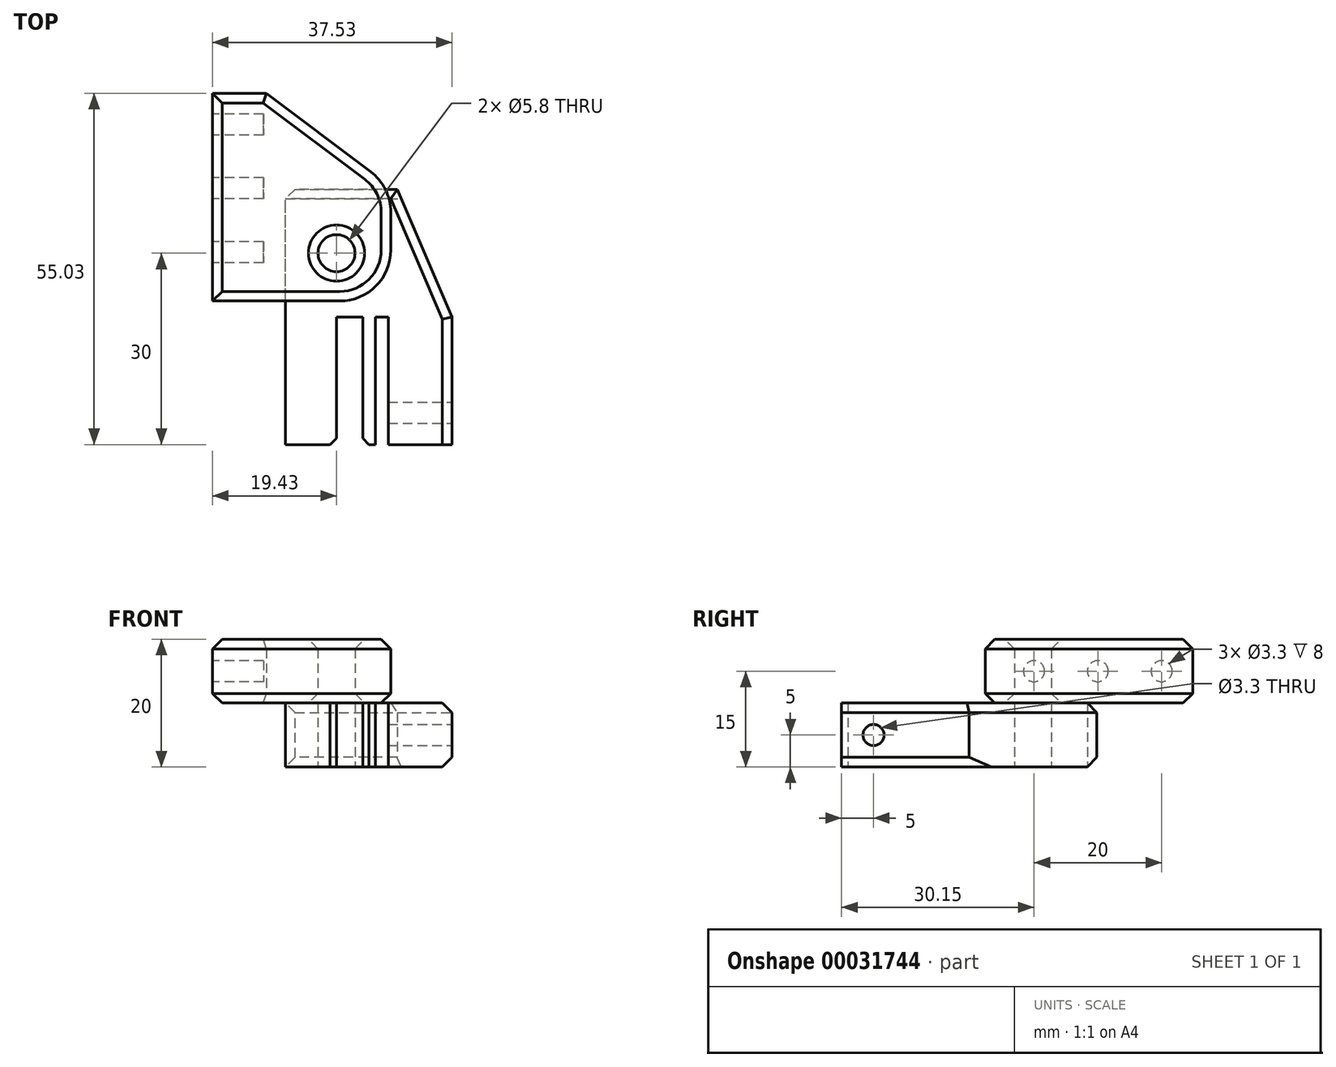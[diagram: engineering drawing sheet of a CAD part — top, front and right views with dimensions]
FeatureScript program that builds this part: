
annotation { "Feature Type Name" : "Feature", "Feature Type Description" : "" }
export const myFeature = defineFeature(function(context is Context, id is Id, definition is map)
    precondition{}
    {
        {
            var Q0;
            Q0=qCreatedBy(makeId("Top.planeOp"),FACE);
            var sketch = newSketch(context, id + "F0", { "sketchPlane" : qUnion([Q0])});
            skLineSegment(sketch, "E0", {"start": v(8, 40) * mm, "end": v(34.1, 40) * mm});
            skLineSegment(sketch, "E1", {"start": v(34.1, 40) * mm, "end": v(34.1, 0) * mm});
            skLineSegment(sketch, "E2", {"start": v(34.1, 0) * mm, "end": v(24.1, 0) * mm});
            skLineSegment(sketch, "E3", {"start": v(24.1, 0) * mm, "end": v(24.1, 20) * mm});
            skLineSegment(sketch, "E4", {"start": v(24.1, 20) * mm, "end": v(22.1, 20) * mm});
            skLineSegment(sketch, "E5", {"start": v(22.1, 20) * mm, "end": v(22.1, 0) * mm});
            skLineSegment(sketch, "E6", {"start": v(22.1, 0) * mm, "end": v(20.1, 0) * mm});
            skLineSegment(sketch, "E7", {"start": v(20.1, 0) * mm, "end": v(20.1, 20) * mm});
            skLineSegment(sketch, "E8", {"start": v(20.1, 20) * mm, "end": v(16, 20) * mm});
            skLineSegment(sketch, "E9", {"start": v(16, 20) * mm, "end": v(16, 0) * mm});
            skLineSegment(sketch, "E10", {"start": v(16, 0) * mm, "end": v(8, 0) * mm});
            skPoint(sketch, "E11.orphan", {"position": v(0, 0) * mm});
            skLineSegment(sketch, "E12", {"start": v(8, 0) * mm, "end": v(8, 40) * mm});
            skSolve(sketch);
        }
        {
            var Q0;
            Q0=qSketchRegion(id+"F0",true);
            extrude(context, id + "F1", {"entities" : qUnion([Q0]), "depth" : 10 * mm});
        }
        {
            var Q0;
            Q0=makeQuery(id+"F1.opExtrude","CAP_FACE",FACE,{"disambiguationData":[OSD([sQuery(id+"F0.wireOp",EDGE,"E0"),sQuery(id+"F0.wireOp",EDGE,"E1"),sQuery(id+"F0.wireOp",EDGE,"E2"),sQuery(id+"F0.wireOp",EDGE,"E3"),sQuery(id+"F0.wireOp",EDGE,"E4"),sQuery(id+"F0.wireOp",EDGE,"E5"),sQuery(id+"F0.wireOp",EDGE,"E6"),sQuery(id+"F0.wireOp",EDGE,"E7"),sQuery(id+"F0.wireOp",EDGE,"E8"),sQuery(id+"F0.wireOp",EDGE,"E9"),sQuery(id+"F0.wireOp",EDGE,"E10"),sQuery(id+"F0.wireOp",EDGE,"5a1ff05f-5f27-4e54-8762-ae27163ca62e")])],"isStart":true});
            var sketch = newSketch(context, id + "F2", { "sketchPlane" : qUnion([Q0])});
            skLineSegment(sketch, "E13", {"start": v(25.5, -40) * mm, "end": v(34.1, -20) * mm});
            skLineSegment(sketch, "E14", {"start": v(34.1, -20) * mm, "end": v(34.1, -40) * mm});
            skLineSegment(sketch, "E15", {"start": v(34.1, -40) * mm, "end": v(25.5, -40) * mm});
            skSolve(sketch);
        }
        {
            var Q0;
            Q0=makeQuery(id+"F2.imprint","IMPRINT",FACE,{"disambiguationData":[TD([[makeQuery(id+"F2.imprint","IMPRINT",EDGE,{"derivedFrom":sQuery(id+"F2.wireOp",EDGE,"E13")}),-1.0]])]});
            extrude(context, id + "F3", {"entities" : qUnion([Q0]), "operationType" : NewBodyOperationType.REMOVE, "oppositeDirection" : true, "depth" : 25 * mm});
        }
        {
            var Q0;
            Q0=makeQuery(id+"F1.opExtrude","SWEPT_FACE",FACE,{"disambiguationData":[OSD([sQuery(id+"F0.wireOp",EDGE,"E1")])]});
            var sketch = newSketch(context, id + "F4", { "sketchPlane" : qUnion([Q0])});
            skCircle(sketch, "E16", {"center": v(5, 5) * mm, "radius": 1.65 * mm});
            skSolve(sketch);
        }
        {
            var Q0;
            Q0=makeQuery(id+"F4.imprint","IMPRINT",FACE,{"disambiguationData":[TD([[makeQuery(id+"F4.imprint","IMPRINT",EDGE,{"derivedFrom":sQuery(id+"F4.wireOp",EDGE,"E16")}),1.0]])]});
            extrude(context, id + "F5", {"entities" : qUnion([Q0]), "operationType" : NewBodyOperationType.REMOVE, "endBound" : BoundingType.UP_TO_NEXT, "oppositeDirection" : true, "depth" : 25 * mm});
        }
        {
            var Q0;
            Q0=makeQuery(id+"F1.opExtrude","CAP_EDGE",EDGE,{"disambiguationData":[OSD([sQuery(id+"F0.wireOp",EDGE,"E0")])],"isStart":false});
            var Q1;
            Q1=makeQuery(id+"F1.opExtrude","CAP_EDGE",EDGE,{"disambiguationData":[OSD([sQuery(id+"F0.wireOp",EDGE,"E0")])],"isStart":true});
            var Q2;
            Q2=makeQuery(id+"F1.opExtrude","CAP_EDGE",EDGE,{"disambiguationData":[OSD([sQuery(id+"F0.wireOp",EDGE,"5a1ff05f-5f27-4e54-8762-ae27163ca62e")])],"isStart":true});
            var Q3;
            Q3=makeQuery(id+"F1.opExtrude","CAP_EDGE",EDGE,{"disambiguationData":[OSD([sQuery(id+"F0.wireOp",EDGE,"5a1ff05f-5f27-4e54-8762-ae27163ca62e")])],"isStart":false});
            var Q4;
            Q4=makeQuery(id+"F1.opExtrude","SWEPT_EDGE",EDGE,{"disambiguationData":[OSD([sQuery(id+"F0.wireOp",EDGE,"E0"),sQuery(id+"F0.wireOp",EDGE,"5a1ff05f-5f27-4e54-8762-ae27163ca62e")])]});
            var Q5;
            Q5=makeQuery(id+"F3.boolean.opBoolean","COPY",EDGE,{"derivedFrom":makeQuery(id+"F3.opExtrude","CAP_EDGE",EDGE,{"disambiguationData":[OSD([sQuery(id+"F2.wireOp",EDGE,"E13")])],"isStart":true})});
            var Q6;
            Q6=makeQuery(id+"F1.opExtrude","CAP_EDGE",EDGE,{"disambiguationData":[OSD([sQuery(id+"F0.wireOp",EDGE,"E1")])],"isStart":true});
            var Q7;
            Q7=makeQuery(id+"F1.opExtrude","CAP_EDGE",EDGE,{"disambiguationData":[OSD([sQuery(id+"F0.wireOp",EDGE,"E1")])],"isStart":false});
            var Q8;
            Q8=makeQuery(id+"F3.boolean.opBoolean","INTERSECT",EDGE,{"derivedFrom":[makeQuery(id+"F1.opExtrude","CAP_FACE",FACE,{"disambiguationData":[OSD([sQuery(id+"F0.wireOp",EDGE,"E0"),sQuery(id+"F0.wireOp",EDGE,"E1"),sQuery(id+"F0.wireOp",EDGE,"E2"),sQuery(id+"F0.wireOp",EDGE,"E3"),sQuery(id+"F0.wireOp",EDGE,"E4"),sQuery(id+"F0.wireOp",EDGE,"E5"),sQuery(id+"F0.wireOp",EDGE,"E6"),sQuery(id+"F0.wireOp",EDGE,"E7"),sQuery(id+"F0.wireOp",EDGE,"E8"),sQuery(id+"F0.wireOp",EDGE,"E9"),sQuery(id+"F0.wireOp",EDGE,"E10"),sQuery(id+"F0.wireOp",EDGE,"5a1ff05f-5f27-4e54-8762-ae27163ca62e")])],"isStart":false}),makeQuery(id+"F3.opExtrude","SWEPT_FACE",FACE,{"disambiguationData":[OSD([sQuery(id+"F2.wireOp",EDGE,"E13")])]})]});
            var Q9;
            Q9=makeQuery(id+"F3.boolean.opBoolean","COPY",EDGE,{"derivedFrom":makeQuery(id+"F3.opExtrude","SWEPT_EDGE",EDGE,{"disambiguationData":[OSD([sQuery(id+"F0.wireOp",EDGE,"E0"),sQuery(id+"F2.wireOp",EDGE,"E13"),sQuery(id+"F2.wireOp",EDGE,"E15")])]})});
            chamfer(context, id + "F6", {"entities" : qUnion([Q0, Q1, Q2, Q3, Q4, Q5, Q6, Q7, Q8, Q9]), "width" : 1.5 * mm, "tangentPropagation" : true});
        }
        {
            var Q0;
            Q0=makeQuery(id+"F1.opExtrude","SWEPT_EDGE",EDGE,{"disambiguationData":[OSD([sQuery(id+"F0.wireOp",EDGE,"E6"),sQuery(id+"F0.wireOp",EDGE,"E7")])]});
            var Q1;
            Q1=makeQuery(id+"F1.opExtrude","SWEPT_EDGE",EDGE,{"disambiguationData":[OSD([sQuery(id+"F0.wireOp",EDGE,"E9"),sQuery(id+"F0.wireOp",EDGE,"E10")])]});
            chamfer(context, id + "F7", {"entities" : qUnion([Q0, Q1]), "width" : 1 * mm, "tangentPropagation" : true});
        }
        {
            var Q0;
            Q0=makeQuery(id+"F1.opExtrude","CAP_FACE",FACE,{"disambiguationData":[OSD([sQuery(id+"F0.wireOp",EDGE,"E0"),sQuery(id+"F0.wireOp",EDGE,"E1"),sQuery(id+"F0.wireOp",EDGE,"E2"),sQuery(id+"F0.wireOp",EDGE,"E3"),sQuery(id+"F0.wireOp",EDGE,"E4"),sQuery(id+"F0.wireOp",EDGE,"E5"),sQuery(id+"F0.wireOp",EDGE,"E6"),sQuery(id+"F0.wireOp",EDGE,"E7"),sQuery(id+"F0.wireOp",EDGE,"E8"),sQuery(id+"F0.wireOp",EDGE,"E9"),sQuery(id+"F0.wireOp",EDGE,"E10"),sQuery(id+"F0.wireOp",EDGE,"E12")])],"isStart":true});
            var sketch = newSketch(context, id + "F8", { "sketchPlane" : qUnion([Q0])});
            skCircle(sketch, "E17", {"center": v(16, -30) * mm, "radius": 2.9 * mm});
            skSolve(sketch);
        }
        {
            var Q0;
            Q0 = qSketchRegion(id + "F8", true);
            extrude(context, id + "F9", {"entities" : qUnion([Q0]), "operationType" : NewBodyOperationType.REMOVE, "oppositeDirection" : true, "depth" : 25 * mm});
        }
        {
            var Q0;
            Q0=makeQuery(id+"F1.opExtrude","CAP_FACE",FACE,{"disambiguationData":[OSD([sQuery(id+"F0.wireOp",EDGE,"E0"),sQuery(id+"F0.wireOp",EDGE,"E1"),sQuery(id+"F0.wireOp",EDGE,"E2"),sQuery(id+"F0.wireOp",EDGE,"E3"),sQuery(id+"F0.wireOp",EDGE,"E4"),sQuery(id+"F0.wireOp",EDGE,"E5"),sQuery(id+"F0.wireOp",EDGE,"E6"),sQuery(id+"F0.wireOp",EDGE,"E7"),sQuery(id+"F0.wireOp",EDGE,"E8"),sQuery(id+"F0.wireOp",EDGE,"E9"),sQuery(id+"F0.wireOp",EDGE,"E10"),sQuery(id+"F0.wireOp",EDGE,"E12")])],"isStart":false});
            var sketch = newSketch(context, id + "F10", { "sketchPlane" : qUnion([Q0])});
            skLineSegment(sketch, "E18", {"start": v(5.02, 40.38) * mm, "end": v(5.02, 40.38) * mm});
            skLineSegment(sketch, "E19", {"start": v(24.51, 40.38) * mm, "end": v(24.51, 22.5) * mm});
            skLineSegment(sketch, "E20", {"start": v(24.51, 22.5) * mm, "end": v(-3.43, 22.5) * mm});
            skLineSegment(sketch, "E21", {"start": v(-3.43, 22.5) * mm, "end": v(-3.43, 55.03) * mm});
            skLineSegment(sketch, "E22", {"start": v(-3.43, 55.03) * mm, "end": v(5.02, 55.03) * mm});
            skCircle(sketch, "E23", {"center": v(16, 30) * mm, "radius": 2.9 * mm});
            skLineSegment(sketch, "E24", {"start": v(5.02, 55.03) * mm, "end": v(24.51, 40.38) * mm});
            skPoint(sketch, "E25.end.orphan", {"position": v(5.02, 40.38) * mm});
            skSolve(sketch);
        }
        {
            var Q0;
            Q0 = qSketchRegion(id + "F10", true);
            extrude(context, id + "F11", {"entities" : qUnion([Q0]), "depth" : 10 * mm});
        }
        {
            var Q0;
            Q0=makeQuery(id+"F11.opExtrude","SWEPT_EDGE",EDGE,{"disambiguationData":[OSD([sQuery(id+"F10.wireOp",EDGE,"E19"),sQuery(id+"F10.wireOp",EDGE,"E24")])]});
            var Q1;
            Q1=makeQuery(id+"F11.opExtrude","SWEPT_EDGE",EDGE,{"disambiguationData":[OSD([sQuery(id+"F10.wireOp",EDGE,"E19"),sQuery(id+"F10.wireOp",EDGE,"E20")])]});
            fillet(context, id + "F12", {"entities" : qUnion([Q0, Q1]), "radius" : 8 * mm, "tangentPropagation" : true, "allowEdgeOverflow" : false});
        }
        {
            var Q0;
            Q0=makeQuery(id+"F11.opExtrude","SWEPT_FACE",FACE,{"disambiguationData":[OSD([sQuery(id+"F10.wireOp",EDGE,"E21")])]});
            var sketch = newSketch(context, id + "F13", { "sketchPlane" : qUnion([Q0])});
            skCircle(sketch, "E26", {"center": v(-50.15, 15) * mm, "radius": 1.65 * mm});
            skCircle(sketch, "E27", {"center": v(-40.15, 15) * mm, "radius": 1.65 * mm});
            skCircle(sketch, "E28", {"center": v(-30.15, 15) * mm, "radius": 1.65 * mm});
            skLineSegment(sketch, "E29", {"start": v(-50.15, 15) * mm, "end": v(-30.15, 15) * mm, "construction": true});
            skSolve(sketch);
        }
        {
            var Q0;
            Q0 = qSketchRegion(id + "F13", true);
            extrude(context, id + "F14", {"entities" : qUnion([Q0]), "operationType" : NewBodyOperationType.REMOVE, "oppositeDirection" : true, "depth" : 8 * mm});
        }
        {
            var Q0;
            Q0=makeQuery(id+"F11.opExtrude","CAP_FACE",FACE,{"disambiguationData":[OSD([sQuery(id+"F10.wireOp",EDGE,"E19"),sQuery(id+"F10.wireOp",EDGE,"E20"),sQuery(id+"F10.wireOp",EDGE,"E21"),sQuery(id+"F10.wireOp",EDGE,"E22"),sQuery(id+"F10.wireOp",EDGE,"E23"),sQuery(id+"F10.wireOp",EDGE,"E24")])],"isStart":true});
            var Q1;
            Q1=makeQuery(id+"F11.opExtrude","CAP_FACE",FACE,{"disambiguationData":[OSD([sQuery(id+"F10.wireOp",EDGE,"E19"),sQuery(id+"F10.wireOp",EDGE,"E20"),sQuery(id+"F10.wireOp",EDGE,"E21"),sQuery(id+"F10.wireOp",EDGE,"E22"),sQuery(id+"F10.wireOp",EDGE,"E23"),sQuery(id+"F10.wireOp",EDGE,"E24")])],"isStart":false});
            chamfer(context, id + "F15", {"entities" : qUnion([Q0, Q1]), "width" : 1.5 * mm, "tangentPropagation" : true});
        }
    });
